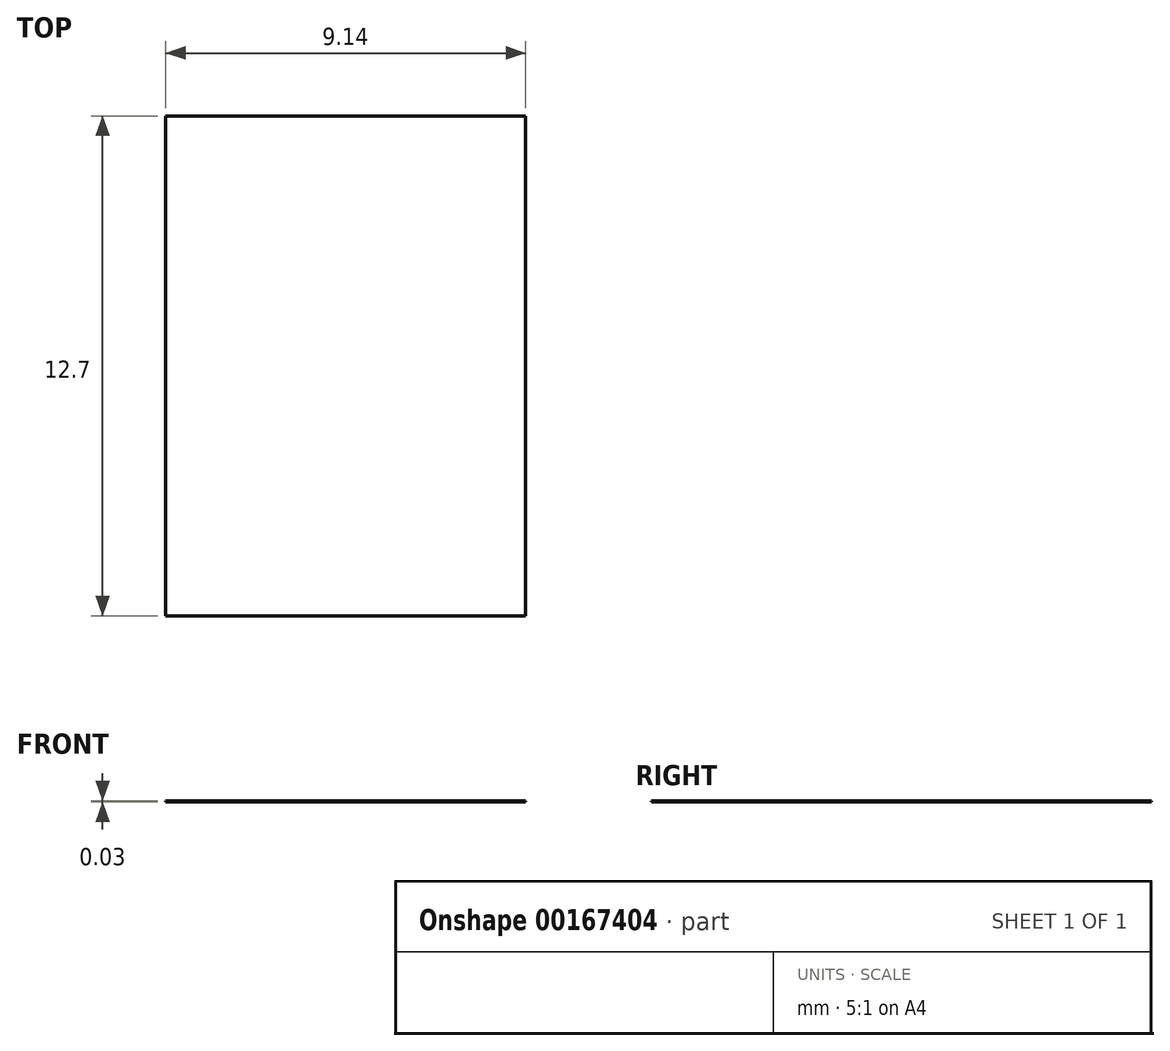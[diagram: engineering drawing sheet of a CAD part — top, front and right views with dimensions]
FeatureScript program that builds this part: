
annotation { "Feature Type Name" : "Feature", "Feature Type Description" : "" }
export const myFeature = defineFeature(function(context is Context, id is Id, definition is map)
    precondition{}
    {
        {
            var Q0;
            Q0=qCreatedBy(makeId("Top.planeOp"),FACE);
            var sketch = newSketch(context, id + "F0", { "sketchPlane" : qUnion([Q0])});
            skLineSegment(sketch, "E0.bottom", {"start": v(4.57, -6.35) * mm, "end": v(-4.57, -6.35) * mm});
            skLineSegment(sketch, "E0.top", {"start": v(4.57, 6.35) * mm, "end": v(-4.57, 6.35) * mm});
            skLineSegment(sketch, "E0.left", {"start": v(4.57, -6.35) * mm, "end": v(4.57, 6.35) * mm});
            skLineSegment(sketch, "E0.right", {"start": v(-4.57, -6.35) * mm, "end": v(-4.57, 6.35) * mm});
            skPoint(sketch, "E0.middle", {"position": v(0, 0) * mm});
            skSolve(sketch);
        }
        {
            var Q0;
            Q0=makeQuery(id+"F0.imprint","IMPRINT",FACE,{"disambiguationData":[TD([[makeQuery(id+"F0.imprint","IMPRINT",EDGE,{"derivedFrom":sQuery(id+"F0.wireOp",EDGE,"E0.bottom")}),-1.0]])]});
            extrude(context, id + "F1", {"entities" : qUnion([Q0]), "depth" : 0.03 * mm});
        }
    });
